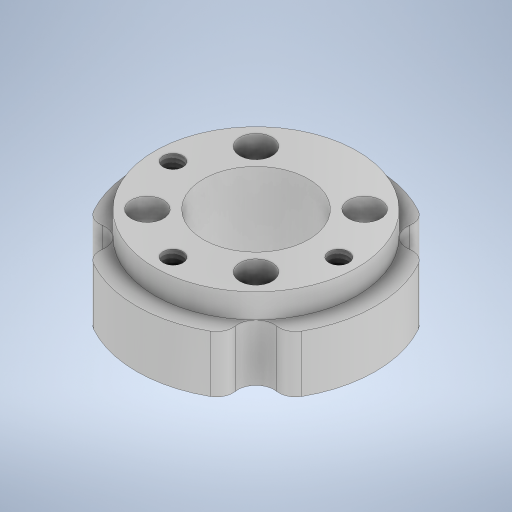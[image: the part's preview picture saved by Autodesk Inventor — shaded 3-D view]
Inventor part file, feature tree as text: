
AUTODESK INVENTOR PART (.ipt)
format: ipt  version: 2024.2 (Build 282272000, 272)  size: 407,040 bytes
history: native  units: mm
features: other x4, hole x3, sketch x2, extrude x2, fillet x1
ambient origin geometry x8: Origin, YZ Plane, XZ Plane, XY Plane, X Axis, Y Axis, Z Axis, Center Point
bodies: Solid1 (feature_tree)
feature tree (12):
  other  "CrossRollerBearingInnerFlange.ipt"
  sketch  "Sketch2"  dims[d6=10.0mm d7=0.0mm d8=3.0mm d9=0.0mm d10=13.0mm d11=2.459mm d12=6.0mm d13=6.5mm d14=3.5mm d15=90.0deg d16=8.0mm d17=20.594885mm d18=2.013mm d19=5.0mm d20=4.0mm d21=3.0mm d22=90.0deg d23=8.0mm d24=20.594885mm d25=4.0mm d26=13.0mm d27=6.0mm d28=5.1mm d29=2.0mm d30=90.0deg d31=8.0mm d32=20.594885mm d33=2.0mm]
  extrude  "Extrusion1"  Depth=10.0mm TaperAngle=360.0deg
  extrude  "Extrusion2"  Depth=3.0mm TaperAngle=0.0deg
  hole  "Hole1"  [1 undecoded]
  hole  "Hole2"  [1 undecoded]
  hole  "Hole3"  [1 undecoded]
  fillet  "Fillet1"  Radius=2.0mm
  other  "TaggingFeature1"
  sketch  "Sketch1"  dims[d0=10.0mm d2=40.0mm d4=360.0deg]
  other  "Solid1::CrossRollerBearingInnerFlange.ipt"
  other  "Srf1"
note: 3 required parameter values undecoded (feature->parameter linkage not recoverable at this tier; creation-order binding heuristic only, values carry confidence <= 0.55)
